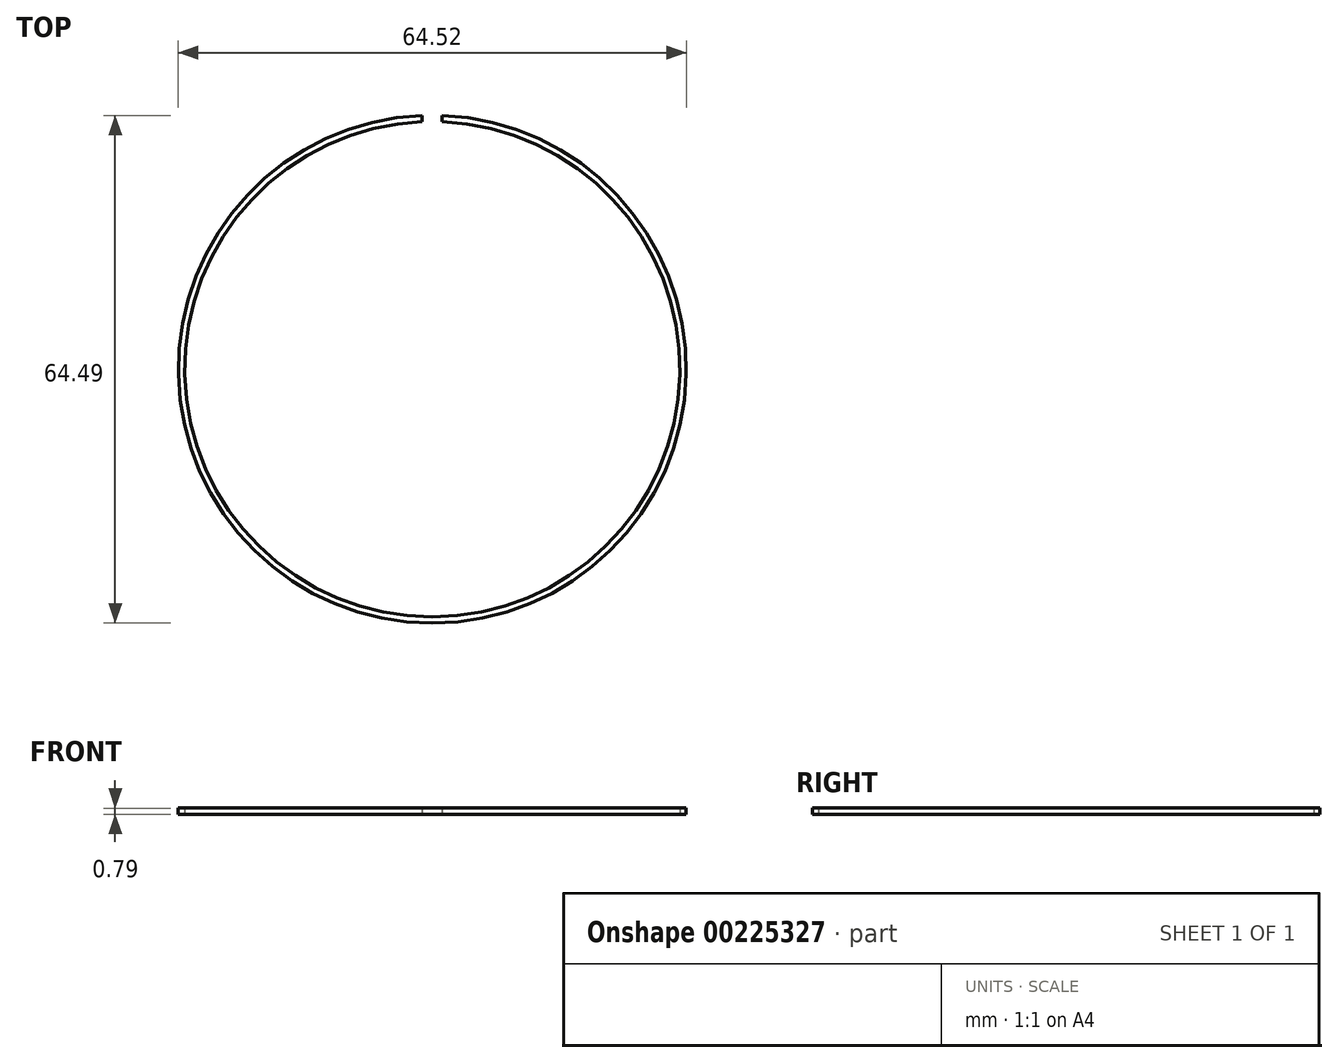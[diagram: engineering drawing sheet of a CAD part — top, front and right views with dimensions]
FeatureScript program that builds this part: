
annotation { "Feature Type Name" : "Feature", "Feature Type Description" : "" }
export const myFeature = defineFeature(function(context is Context, id is Id, definition is map)
    precondition{}
    {
        {
            var Q0;
            Q0=qCreatedBy(makeId("Top.planeOp"),FACE);
            var sketch = newSketch(context, id + "F0", { "sketchPlane" : qUnion([Q0])});
            skArc(sketch, "E0", {"start": v(-1.27, 32.23) * mm, "mid": v(0, -32.26) * mm, "end": v(1.27, 32.23) * mm});
            skArc(sketch, "E1.0", {"start": v(-1.27, 31.44) * mm, "mid": v(0, -31.46) * mm, "end": v(1.27, 31.44) * mm});
            skLineSegment(sketch, "E2", {"start": v(-1.27, 32.23) * mm, "end": v(-1.27, 31.44) * mm});
            skLineSegment(sketch, "E3", {"start": v(1.27, 32.23) * mm, "end": v(1.27, 31.44) * mm});
            skSolve(sketch);
        }
        {
            var Q0;
            Q0 = qSketchRegion(id + "F0", true);
            extrude(context, id + "F1", {"entities" : qUnion([Q0]), "depth" : 0.8 * mm});
        }
    });
